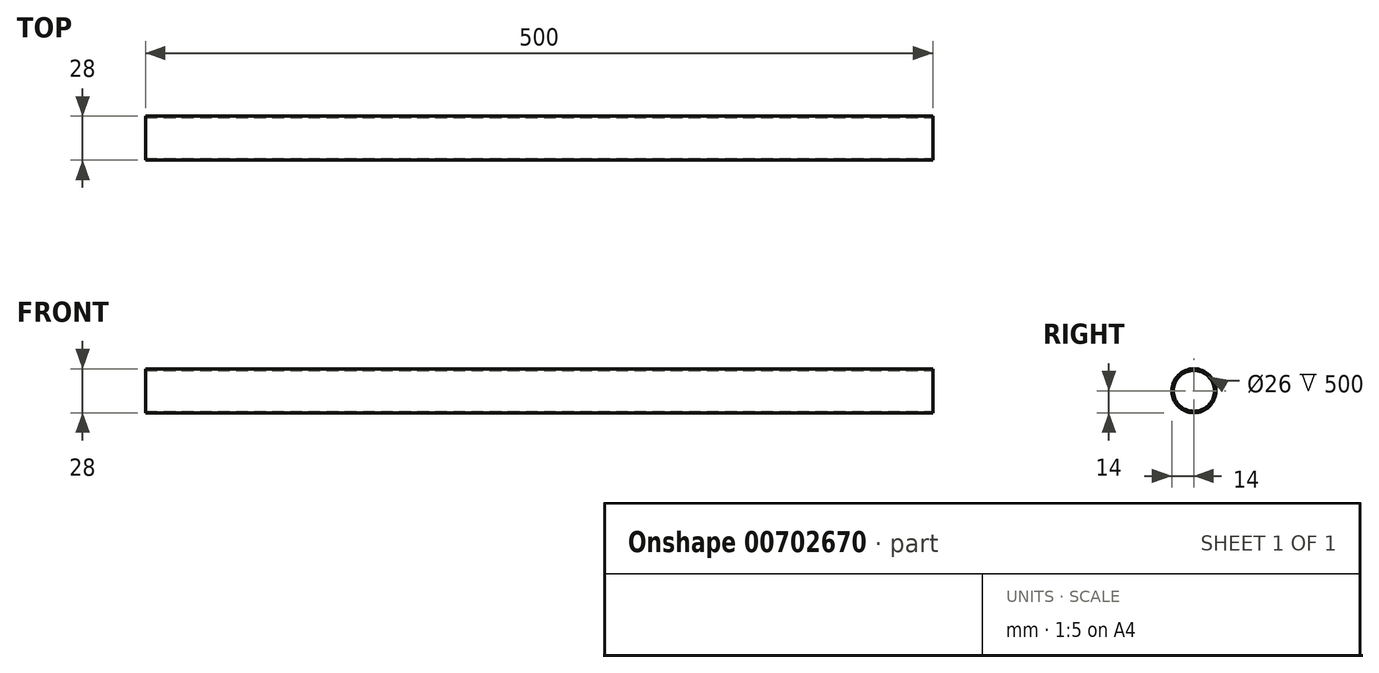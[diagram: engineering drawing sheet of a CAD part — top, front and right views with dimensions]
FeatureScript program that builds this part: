
annotation { "Feature Type Name" : "Feature", "Feature Type Description" : "" }
export const myFeature = defineFeature(function(context is Context, id is Id, definition is map)
    precondition{}
    {
        {
            var Q0;
            Q0=qCreatedBy(makeId("Right.planeOp"),FACE);
            var sketch = newSketch(context, id + "F0", { "sketchPlane" : qUnion([Q0])});
            skCircle(sketch, "E0", {"center": v(0, 0) * mm, "radius": 14 * mm});
            skCircle(sketch, "E1", {"center": v(0, 0) * mm, "radius": 13 * mm});
            skSolve(sketch);
        }
        {
            var Q0;
            Q0=makeQuery(id+"F0.imprint","IMPRINT",FACE,{"disambiguationData":[TD([[makeQuery(id+"F0.imprint","IMPRINT",EDGE,{"derivedFrom":sQuery(id+"F0.wireOp",EDGE,"E0")}),1.0]])]});
            extrude(context, id + "F1", {"entities" : qUnion([Q0]), "oppositeDirection" : true, "depth" : 500 * mm, "offsetDistance" : 25.4 * mm});
        }
    });
